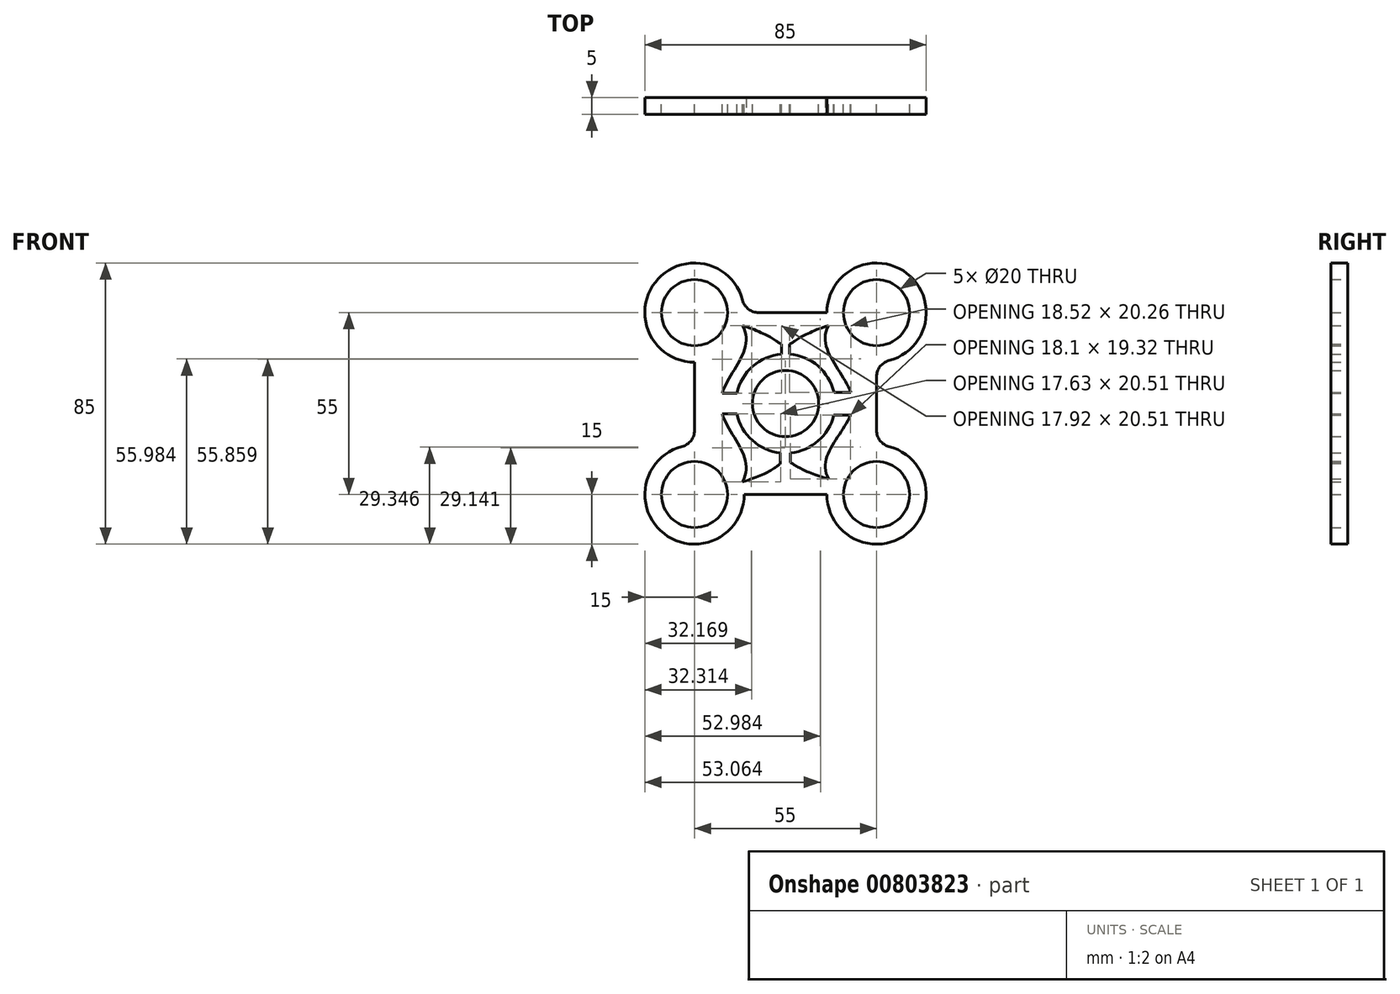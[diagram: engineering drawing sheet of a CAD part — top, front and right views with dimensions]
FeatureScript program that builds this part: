
annotation { "Feature Type Name" : "Feature", "Feature Type Description" : "" }
export const myFeature = defineFeature(function(context is Context, id is Id, definition is map)
    precondition{}
    {
        {
            var Q0;
            Q0=qCreatedBy(makeId("Front.planeOp"),FACE);
            var sketch = newSketch(context, id + "F0", { "sketchPlane" : qUnion([Q0])});
            skCircle(sketch, "E0", {"center": v(27.5, 27.5) * mm, "radius": 15 * mm});
            skCircle(sketch, "E1.1.0", {"center": v(-27.5, 27.5) * mm, "radius": 15 * mm});
            skCircle(sketch, "E1.2.0", {"center": v(-27.5, -27.5) * mm, "radius": 15 * mm});
            skCircle(sketch, "E1.3.0", {"center": v(27.5, -27.5) * mm, "radius": 15 * mm});
            skPoint(sketch, "E2.center", {"position": v(0, 0) * mm});
            skCircle(sketch, "E3", {"center": v(0, 0) * mm, "radius": 38.9 * mm, "construction": true});
            skLineSegment(sketch, "E4", {"start": v(-12.5, -27.5) * mm, "end": v(12.5, -27.5) * mm});
            skLineSegment(sketch, "E5", {"start": v(27.5, 12.5) * mm, "end": v(27.5, -12.5) * mm});
            skLineSegment(sketch, "E6", {"start": v(12.5, 27.5) * mm, "end": v(-12.5, 27.5) * mm});
            skLineSegment(sketch, "E7", {"start": v(-27.5, 12.5) * mm, "end": v(-27.5, -12.5) * mm});
            skCircle(sketch, "E8", {"center": v(0, 0) * mm, "radius": 15 * mm});
            skCircle(sketch, "E9", {"center": v(0, 0) * mm, "radius": 10 * mm});
            skFitSpline(sketch, "E10", {"points": [v(13.01, -22.81) * mm, v(20.38, 0) * mm, v(13.01, 23.62) * mm], "startDerivative": vector(-27.18, 47.54) * mm, "endDerivative": vector(27.17, 47.55) * mm});
            skFitSpline(sketch, "E11", {"points": [v(13.01, 23.62) * mm, v(0, 17.48) * mm, v(-13.01, 23.62) * mm], "startDerivative": vector(-58.42, -18.94) * mm, "endDerivative": vector(-58.42, 18.94) * mm});
            skFitSpline(sketch, "E12", {"points": [v(-13.01, 23.62) * mm, v(-19.68, 0) * mm, v(-13.01, -23.62) * mm], "startDerivative": vector(28.6, -47.59) * mm, "endDerivative": vector(-28.6, -47.59) * mm});
            skFitSpline(sketch, "E13", {"points": [v(-13.01, -23.62) * mm, v(0, -17.34) * mm, v(13.01, -22.81) * mm], "startDerivative": vector(58.42, 15.75) * mm, "endDerivative": vector(58.42, -15.75) * mm});
            skLineSegment(sketch, "E14", {"start": v(-1.52, -18.15) * mm, "end": v(-1.52, -14.92) * mm});
            skLineSegment(sketch, "E15", {"start": v(14.59, -3.5) * mm, "end": v(19.61, -3.5) * mm});
            skLineSegment(sketch, "E16", {"start": v(-1.23, 14.95) * mm, "end": v(-1.23, 17.92) * mm});
            skLineSegment(sketch, "E17", {"start": v(-14.68, -3.1) * mm, "end": v(-19.15, -3.1) * mm});
            skLineSegment(sketch, "E18", {"start": v(20.38, 0) * mm, "end": v(15, 0) * mm, "construction": true});
            skLineSegment(sketch, "E19", {"start": v(0, 17.48) * mm, "end": v(0, 15) * mm, "construction": true});
            skLineSegment(sketch, "E20", {"start": v(-19.68, 0) * mm, "end": v(-15, 0) * mm, "construction": true});
            skLineSegment(sketch, "E21", {"start": v(0, -17.34) * mm, "end": v(0, -15) * mm, "construction": true});
            skLineSegment(sketch, "E22.MirrorCS", {"start": v(1.52, -18.15) * mm, "end": v(1.52, -14.92) * mm});
            skLineSegment(sketch, "E23.MirrorCS", {"start": v(1.23, 14.95) * mm, "end": v(1.23, 17.92) * mm});
            skLineSegment(sketch, "E24.MirrorCS", {"start": v(-14.68, 3.1) * mm, "end": v(-19.15, 3.1) * mm});
            skLineSegment(sketch, "E25", {"start": v(19.74, 3.35) * mm, "end": v(14.62, 3.35) * mm});
            skCircle(sketch, "E26", {"center": v(-27.5, -27.5) * mm, "radius": 10 * mm});
            skCircle(sketch, "E27", {"center": v(-27.5, 27.5) * mm, "radius": 10 * mm});
            skCircle(sketch, "E28", {"center": v(27.5, 27.5) * mm, "radius": 10 * mm});
            skCircle(sketch, "E29", {"center": v(27.5, -27.5) * mm, "radius": 10 * mm});
            skSolve(sketch);
        }
        {
            var Q0;
            {var subQ0=sQuery(id+"F0.wireOp",EDGE,"E15");Q0=makeQuery(id+"F0.imprint","IMPRINT",FACE,{"disambiguationData":[TD([[makeQuery(id+"F0.imprint","IMPRINT",EDGE,{"derivedFrom":subQ0}),1.0]])]});}
            var Q1;
            {var subQ0=sQuery(id+"F0.wireOp",EDGE,"E14");Q1=makeQuery(id+"F0.imprint","IMPRINT",FACE,{"disambiguationData":[TD([[makeQuery(id+"F0.imprint","IMPRINT",EDGE,{"derivedFrom":subQ0}),-1.0]])]});}
            var Q2;
            {var subQ0=sQuery(id+"F0.wireOp",EDGE,"E17");Q2=makeQuery(id+"F0.imprint","IMPRINT",FACE,{"disambiguationData":[TD([[makeQuery(id+"F0.imprint","IMPRINT",EDGE,{"derivedFrom":subQ0}),-1.0]])]});}
            var Q3;
            {var subQ0=sQuery(id+"F0.wireOp",EDGE,"E16");Q3=makeQuery(id+"F0.imprint","IMPRINT",FACE,{"disambiguationData":[TD([[makeQuery(id+"F0.imprint","IMPRINT",EDGE,{"derivedFrom":subQ0}),-1.0]])]});}
            var Q4;
            {var subQ10=sQuery(id+"F0.wireOp",EDGE,"E4");Q4=makeQuery(id+"F0.imprint","IMPRINT",FACE,{"disambiguationData":[TD([[makeQuery(id+"F0.imprint","IMPRINT",EDGE,{"derivedFrom":subQ10}),1.0]])]});}
            var Q5;
            {var subQ4=sQuery(id+"F0.wireOp",EDGE,"E7");Q5=makeQuery(id+"F0.imprint","IMPRINT",FACE,{"disambiguationData":[TD([[makeQuery(id+"F0.imprint","IMPRINT",EDGE,{"derivedFrom":subQ4}),1.0]])]});}
            var Q6;
            {var subQ4=sQuery(id+"F0.wireOp",EDGE,"E6");Q6=makeQuery(id+"F0.imprint","IMPRINT",FACE,{"disambiguationData":[TD([[makeQuery(id+"F0.imprint","IMPRINT",EDGE,{"derivedFrom":subQ4}),1.0]])]});}
            var Q7;
            {var subQ0=sQuery(id+"F0.wireOp",EDGE,"E0");var subQ3=makeQuery(id+"F0.imprint","INTERSECT",VERTEX,{"derivedFrom":[subQ0,sQuery(id+"F0.wireOp",EDGE,"E5")]});Q7=makeQuery(id+"F0.imprint","IMPRINT",FACE,{"disambiguationData":[TD([[makeQuery(id+"F0.imprint","IMPRINT",EDGE,{"disambiguationData":[TD([[subQ3,-1.0]])],"derivedFrom":subQ0}),1.0]])]});}
            var Q8;
            Q8=makeQuery(id+"F0.imprint","IMPRINT",FACE,{"disambiguationData":[TD([[makeQuery(id+"F0.imprint","IMPRINT",EDGE,{"derivedFrom":sQuery(id+"F0.wireOp",EDGE,"E9")}),-1.0]])]});
            var Q9;
            {var subQ0=sQuery(id+"F0.wireOp",EDGE,"E1.3.0");var subQ1=makeQuery(id+"F0.imprint","INTERSECT",VERTEX,{"derivedFrom":[subQ0,sQuery(id+"F0.wireOp",EDGE,"E4")]});Q9=makeQuery(id+"F0.imprint","IMPRINT",FACE,{"disambiguationData":[TD([[makeQuery(id+"F0.imprint","IMPRINT",EDGE,{"disambiguationData":[TD([[subQ1,1.0]])],"derivedFrom":subQ0}),1.0]])]});}
            var Q10;
            {var subQ0=sQuery(id+"F0.wireOp",EDGE,"E1.2.0");var subQ1=makeQuery(id+"F0.imprint","INTERSECT",VERTEX,{"derivedFrom":[subQ0,sQuery(id+"F0.wireOp",EDGE,"E4")]});Q10=makeQuery(id+"F0.imprint","IMPRINT",FACE,{"disambiguationData":[TD([[makeQuery(id+"F0.imprint","IMPRINT",EDGE,{"disambiguationData":[TD([[subQ1,1.0]])],"derivedFrom":subQ0}),1.0]])]});}
            var Q11;
            {var subQ0=sQuery(id+"F0.wireOp",EDGE,"E1.1.0");var subQ3=makeQuery(id+"F0.imprint","INTERSECT",VERTEX,{"derivedFrom":[subQ0,sQuery(id+"F0.wireOp",EDGE,"E6")]});Q11=makeQuery(id+"F0.imprint","IMPRINT",FACE,{"disambiguationData":[TD([[makeQuery(id+"F0.imprint","IMPRINT",EDGE,{"disambiguationData":[TD([[subQ3,-1.0]])],"derivedFrom":subQ0}),1.0]])]});}
            extrude(context, id + "F1", {"entities" : qUnion([Q0, Q1, Q2, Q3, Q4, Q5, Q6, Q7, Q8, Q9, Q10, Q11]), "depth" : 5 * mm, "offsetDistance" : 25 * mm});
        }
        {
            var Q0;
            Q0=makeQuery(id+"F1.opExtrude","SWEPT_EDGE",EDGE,{"disambiguationData":[OSD([sQuery(id+"F0.wireOp",EDGE,"E1.3.0"),sQuery(id+"F0.wireOp",EDGE,"E5")])]});
            fillet(context, id + "F2", {"entities" : qUnion([Q0]), "radius" : 5 * mm, "tangentPropagation" : true, "allowEdgeOverflow" : false});
        }
        {
            var Q0;
            Q0=makeQuery(id+"F1.opExtrude","SWEPT_EDGE",EDGE,{"disambiguationData":[OSD([sQuery(id+"F0.wireOp",EDGE,"E1.2.0"),sQuery(id+"F0.wireOp",EDGE,"E7")])]});
            var Q1;
            Q1=makeQuery(id+"F1.opExtrude","SWEPT_EDGE",EDGE,{"disambiguationData":[OSD([sQuery(id+"F0.wireOp",EDGE,"E1.1.0"),sQuery(id+"F0.wireOp",EDGE,"E6")])]});
            var Q2;
            Q2=makeQuery(id+"F1.opExtrude","SWEPT_EDGE",EDGE,{"disambiguationData":[OSD([sQuery(id+"F0.wireOp",EDGE,"E0"),sQuery(id+"F0.wireOp",EDGE,"E5")])]});
            fillet(context, id + "F3", {"entities" : qUnion([Q0, Q1, Q2]), "radius" : 5 * mm, "tangentPropagation" : true, "allowEdgeOverflow" : false});
        }
        {
            var Q0;
            Q0=makeQuery(id+"F0.imprint","IMPRINT",FACE,{"disambiguationData":[TD([[makeQuery(id+"F0.imprint","IMPRINT",EDGE,{"derivedFrom":sQuery(id+"F0.wireOp",EDGE,"E9")}),1.0]])]});
            extrude(context, id + "F4", {"entities" : qUnion([Q0]), "depth" : 25 * mm, "offsetDistance" : 25 * mm});
        }
        {
            var Q0;
            Q0=makeQuery(id+"F4.opExtrude","SWEPT_BODY",BODY,{"disambiguationData":[OSD([sQuery(id+"F0.wireOp",EDGE,"E9")])]});
            deleteBodies(context, id + "F5", {"entities" : qUnion([Q0])});
        }
    });
